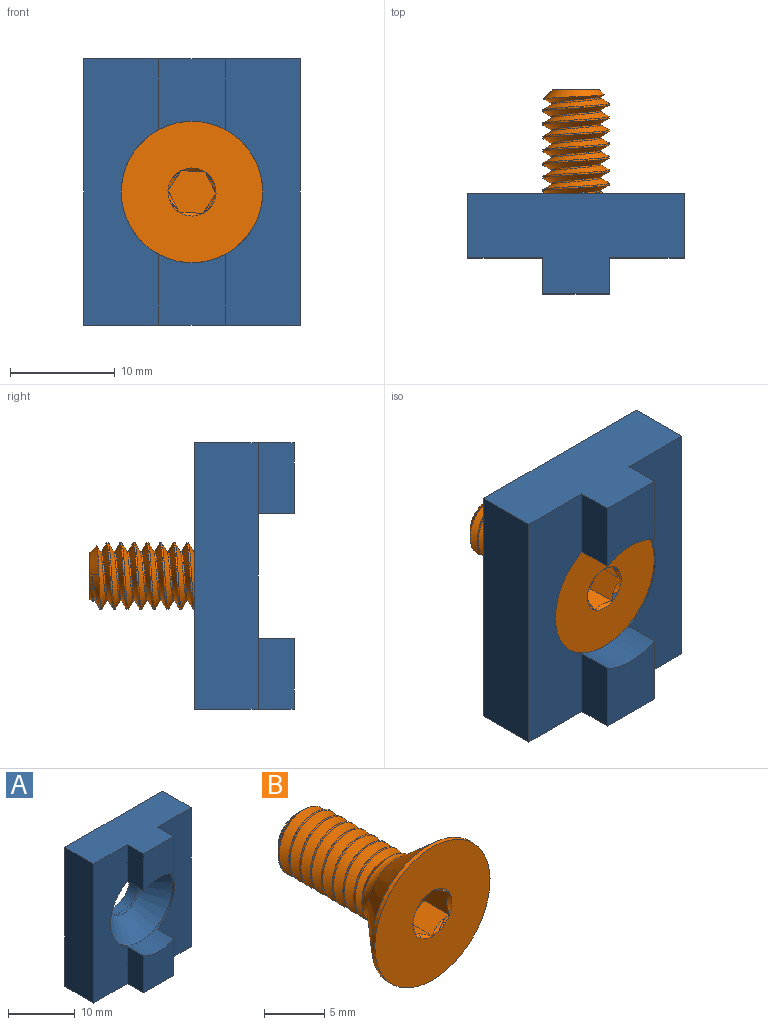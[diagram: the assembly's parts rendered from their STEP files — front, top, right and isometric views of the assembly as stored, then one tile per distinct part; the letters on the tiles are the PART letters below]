
ASSEMBLY  parts=2 mates=1
PART A: 17 faces, bbox 20.6x9.5x25.4 mm
  f0: plane 25.4x20.62mm, normal (0,1,0), area 488mm2, adj f9,f10,f11,f12,f14
  f1: plane 25.4x7.14mm, normal (0,-1,0), area 151mm2, adj f2,f3,f10,f11,f12,f13
  f2: plane 6.75x3.43mm, normal (1,0,0), area 23.1mm2, adj f1,f5,f12,f13
  f3: plane 6.75x3.43mm, normal (1,0,0), area 23.1mm2, adj f1,f4,f11,f13
  f4: plane 6.75x6.35mm, normal (0,-1,0), area 39.5mm2, adj f3,f6,f11,f13
  f5: plane 6.75x6.35mm, normal (0,-1,0), area 39.5mm2, adj f2,f7,f12,f13
  f6: plane 6.75x3.43mm, normal (-1,0,0), area 23.1mm2, adj f4,f8,f11,f13
  f7: plane 6.75x3.43mm, normal (-1,0,0), area 23.1mm2, adj f5,f8,f12,f13
  f8: plane 25.4x7.14mm, normal (0,-1,0), area 151mm2, adj f6,f7,f9,f11,f12,f13
  f9: plane 25.4x6.1mm, normal (-1,0,0), area 154.8mm2, adj f0,f8,f11,f12
  f10: plane 25.4x6.1mm, normal (1,0,0), area 154.8mm2, adj f0,f1,f11,f12
  f11: plane 20.62x9.53mm, normal (0,0,-1), area 147.5mm2, adj f0,f1,f3,f4,f6,f8,f9,f10
  f12: plane 20.62x9.53mm, normal (0,0,1), area 147.5mm2, adj f0,f1,f2,f5,f7,f8,f9,f10
  f13: cylinder r=6.74mm len=13.49mm, axis (0,-1,0), area 62.7mm2, adj f1,f2,f3,f4,f5,f6,f7,f8
  f14: cylinder r=3.38mm len=6.76mm, axis (0,-1,0), area 37.7mm2, adj f0,f15
  f15: torus R=4.68mm, axis (0,-1,0), area 6.2mm2, adj f14,f16
  f16: cone r=3.54mm half-angle=41deg, axis (0,-1,0), area 157.6mm2, adj f13,f15
PART B: 25 faces, bbox 14.4x17.3x14.4 mm
  f0: plane 14.23x14.23mm, normal (0,-1,0), area 126.4mm2, adj f11,f12,f13,f14,f15,f16,f17
  f1: bspline ~10.99x6.49mm, area 128.6mm2, adj f2,f4,f5,f6,f8
  f2: cylinder r=2.35mm len=9.84mm, axis (0,1,0), area 18.2mm2, adj f1,f3,f5,f8
  f3: bspline ~11.95x6.49mm, area 128.4mm2, adj f2,f4,f5,f6,f8
  f4: cylinder r=3.17mm len=9.84mm, axis (0,-1,0), area 24.7mm2, adj f1,f3,f6,f9
  f5: cone r=2.21mm half-angle=45deg, axis (0,-1,0), area 10.1mm2, adj f1,f2,f3,f6,f7
  f6: cone r=2.21mm half-angle=45deg, axis (0,-1,0), area 2.4mm2, adj f1,f3,f4,f5
  f7: plane 4.43x4.43mm, normal (0,1,0), area 15.4mm2, adj f5
  f8: cone r=0mm half-angle=45deg, axis (0,-1,0), area 10.5mm2, adj f1,f2,f3,f9
  f9: torus R=4.68mm, axis (0,-1,0), area 22.3mm2, adj f4,f8,f10
  f10: cone r=3.54mm half-angle=41deg, axis (0,-1,0), area 157.6mm2, adj f9,f11
  f11: cylinder r=6.74mm len=13.49mm, axis (0,-1,0), area 17.3mm2, adj f0,f10
  f12: cone r=2.29mm half-angle=45deg, axis (0,-1,0), area 0mm2, adj f0,f19
  f13: cone r=2.29mm half-angle=45deg, axis (0,-1,0), area 0mm2, adj f0,f20
  f14: cone r=2.29mm half-angle=45deg, axis (0,-1,0), area 0mm2, adj f0,f21
  f15: cone r=2.29mm half-angle=45deg, axis (0,-1,0), area 0mm2, adj f0,f22
  f16: cone r=2.29mm half-angle=45deg, axis (0,-1,0), area 0mm2, adj f0,f23
  f17: cone r=2.29mm half-angle=45deg, axis (0,-1,0), area 0mm2, adj f0,f24
  f18: plane 4.58x3.97mm, normal (0,-1,0), area 13.6mm2, adj f19,f20,f21,f22,f23,f24
  f19: plane 3.85x3.16mm, normal (-1,0,0), area 6.4mm2, adj f12,f18,f20,f24
  f20: plane 3.84x2.85mm, normal (-0.5,0,-0.87), area 6.4mm2, adj f13,f18,f19,f21
  f21: plane 3.84x2.85mm, normal (0.5,0,-0.87), area 6.4mm2, adj f14,f18,f20,f22
  f22: plane 3.85x3.16mm, normal (1,0,0), area 6.4mm2, adj f15,f18,f21,f23
  f23: plane 3.84x2.85mm, normal (0.5,0,0.87), area 6.4mm2, adj f16,f18,f22,f24
  f24: plane 3.84x2.85mm, normal (-0.5,0,0.87), area 6.4mm2, adj f17,f18,f19,f23
PLACE A t=(3.53,6.58,4.27)mm fixed
PLACE B rot(axis=(0,-1,0),87.4deg) t=(3.53,6.73,4.27)mm
MATE revolute A.f13 <-> B.f4  axis (0,-1,0) through (3.53,6.99,4.27)mm
